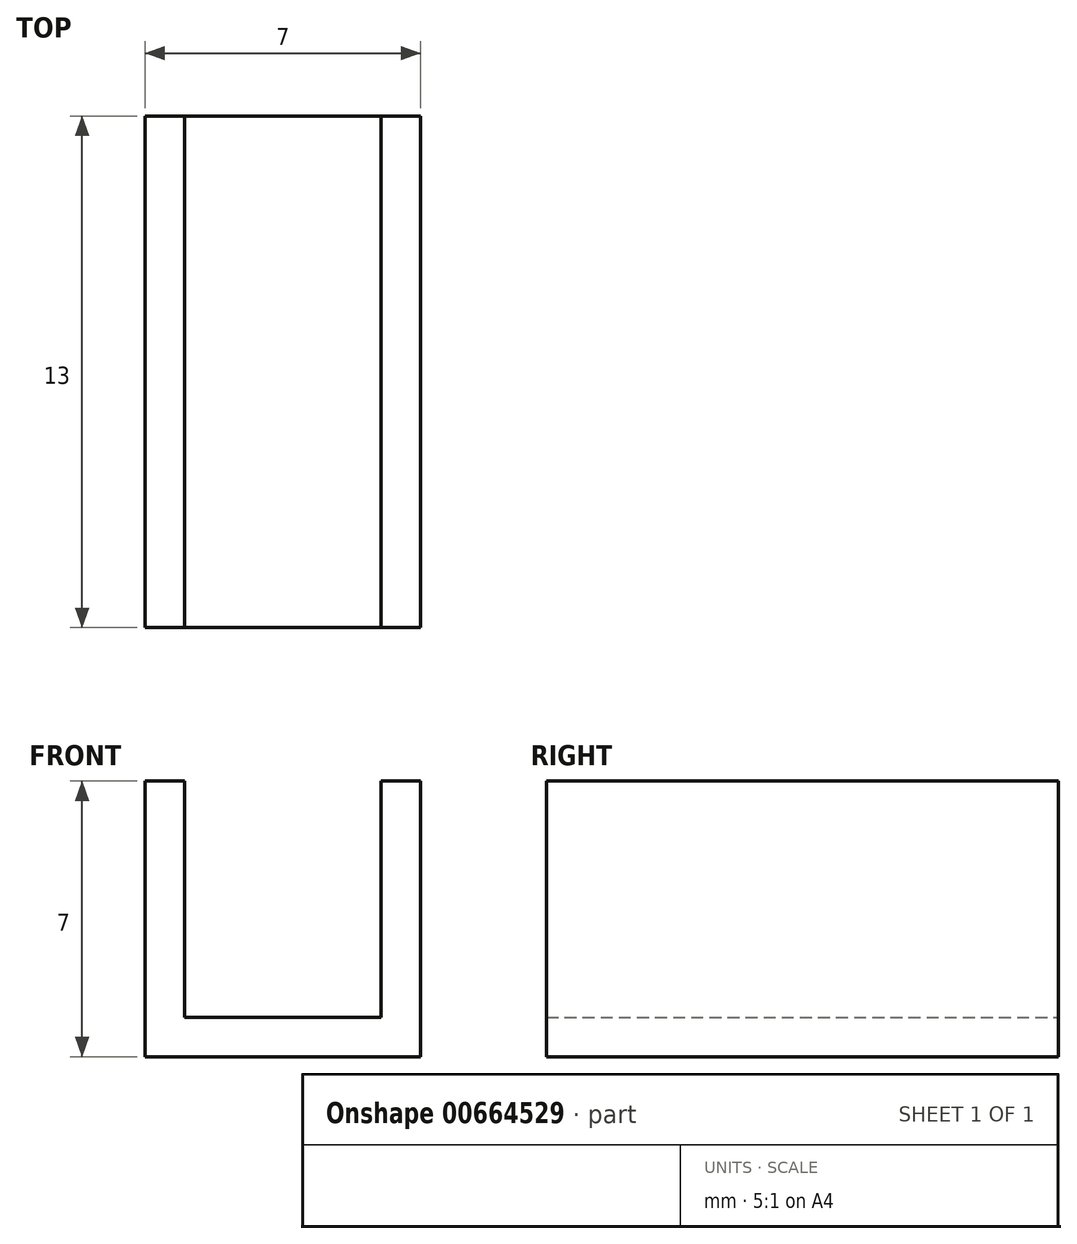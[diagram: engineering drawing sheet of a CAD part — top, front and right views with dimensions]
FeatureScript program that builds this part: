
annotation { "Feature Type Name" : "Feature", "Feature Type Description" : "" }
export const myFeature = defineFeature(function(context is Context, id is Id, definition is map)
    precondition{}
    {
        {
            var Q0;
            Q0=qCreatedBy(makeId("Front.planeOp"),FACE);
            var sketch = newSketch(context, id + "F0", { "sketchPlane" : qUnion([Q0])});
            skLineSegment(sketch, "E0.bottom", {"start": v(3.5, 3.5) * mm, "end": v(-3.5, 3.5) * mm});
            skLineSegment(sketch, "E0.top", {"start": v(3.5, -3.5) * mm, "end": v(-3.5, -3.5) * mm});
            skLineSegment(sketch, "E0.left", {"start": v(3.5, 3.5) * mm, "end": v(3.5, -3.5) * mm});
            skLineSegment(sketch, "E0.right", {"start": v(-3.5, 3.5) * mm, "end": v(-3.5, -3.5) * mm});
            skPoint(sketch, "E0.middle", {"position": v(0, 0) * mm});
            skLineSegment(sketch, "E1.bottom", {"start": v(-2.5, 3.5) * mm, "end": v(2.5, 3.5) * mm});
            skLineSegment(sketch, "E1.top", {"start": v(-2.5, -2.5) * mm, "end": v(2.5, -2.5) * mm});
            skLineSegment(sketch, "E1.left", {"start": v(-2.5, 3.5) * mm, "end": v(-2.5, -2.5) * mm});
            skLineSegment(sketch, "E1.right", {"start": v(2.5, 3.5) * mm, "end": v(2.5, -2.5) * mm});
            skSolve(sketch);
        }
        {
            var Q0;
            Q0=makeQuery(id+"F0.imprint","IMPRINT",FACE,{"disambiguationData":[TD([[makeQuery(id+"F0.imprint","IMPRINT",EDGE,{"derivedFrom":sQuery(id+"F0.wireOp",EDGE,"E0.top")}),-1.0]])]});
            extrude(context, id + "F1", {"entities" : qUnion([Q0]), "depth" : 13 * mm, "offsetDistance" : 25 * mm});
        }
    });
